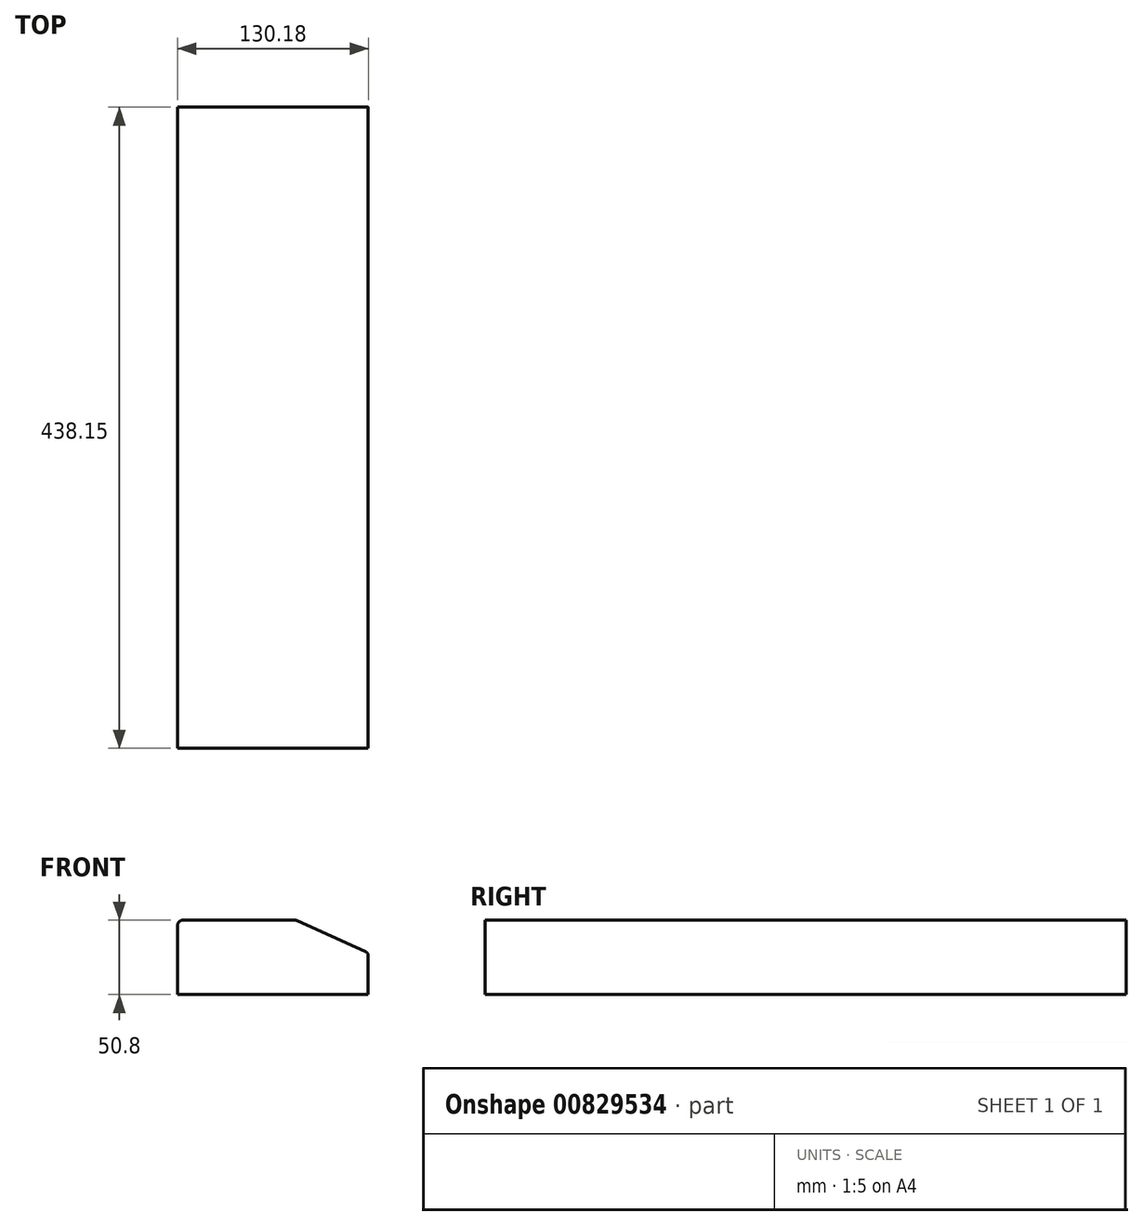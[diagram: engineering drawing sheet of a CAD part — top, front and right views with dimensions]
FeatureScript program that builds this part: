
annotation { "Feature Type Name" : "Feature", "Feature Type Description" : "" }
export const myFeature = defineFeature(function(context is Context, id is Id, definition is map)
    precondition{}
    {
        {
            var Q0;
            Q0=qCreatedBy(makeId("Front.planeOp"),FACE);
            var sketch = newSketch(context, id + "F0", { "sketchPlane" : qUnion([Q0])});
            skLineSegment(sketch, "E0", {"start": v(0, 0) * mm, "end": v(0, 47.62) * mm});
            skLineSegment(sketch, "E1", {"start": v(3.17, 50.8) * mm, "end": v(80.27, 50.8) * mm});
            skLineSegment(sketch, "E2", {"start": v(81.57, 50.52) * mm, "end": v(128.3, 29.42) * mm});
            skLineSegment(sketch, "E3", {"start": v(130.18, 26.52) * mm, "end": v(130.18, 0) * mm});
            skLineSegment(sketch, "E4", {"start": v(130.17, 0) * mm, "end": v(0, 0) * mm});
            skPoint(sketch, "E5.visualSharp", {"position": v(0, 50.8) * mm});
            skArc(sketch, "E5.filletArc", {"start": v(3.17, 50.8) * mm, "mid": v(0.93, 49.87) * mm, "end": v(0, 47.63) * mm});
            skPoint(sketch, "E6.visualSharp", {"position": v(80.95, 50.8) * mm});
            skArc(sketch, "E6.filletArc", {"start": v(81.57, 50.52) * mm, "mid": v(80.93, 50.73) * mm, "end": v(80.27, 50.8) * mm});
            skPoint(sketch, "E7.visualSharp", {"position": v(130.18, 28.58) * mm});
            skArc(sketch, "E7.filletArc", {"start": v(130.18, 26.52) * mm, "mid": v(129.67, 28.25) * mm, "end": v(128.3, 29.42) * mm});
            skSolve(sketch);
        }
        {
            var Q0;
            Q0=makeQuery(id+"F0.imprint","IMPRINT",FACE,{"disambiguationData":[TD([[makeQuery(id+"F0.imprint","IMPRINT",EDGE,{"derivedFrom":sQuery(id+"F0.wireOp",EDGE,"E0")}),-1.0]])]});
            extrude(context, id + "F1", {"entities" : qUnion([Q0]), "depth" : 438.15 * mm, "offsetDistance" : 25.4 * mm});
        }
    });
